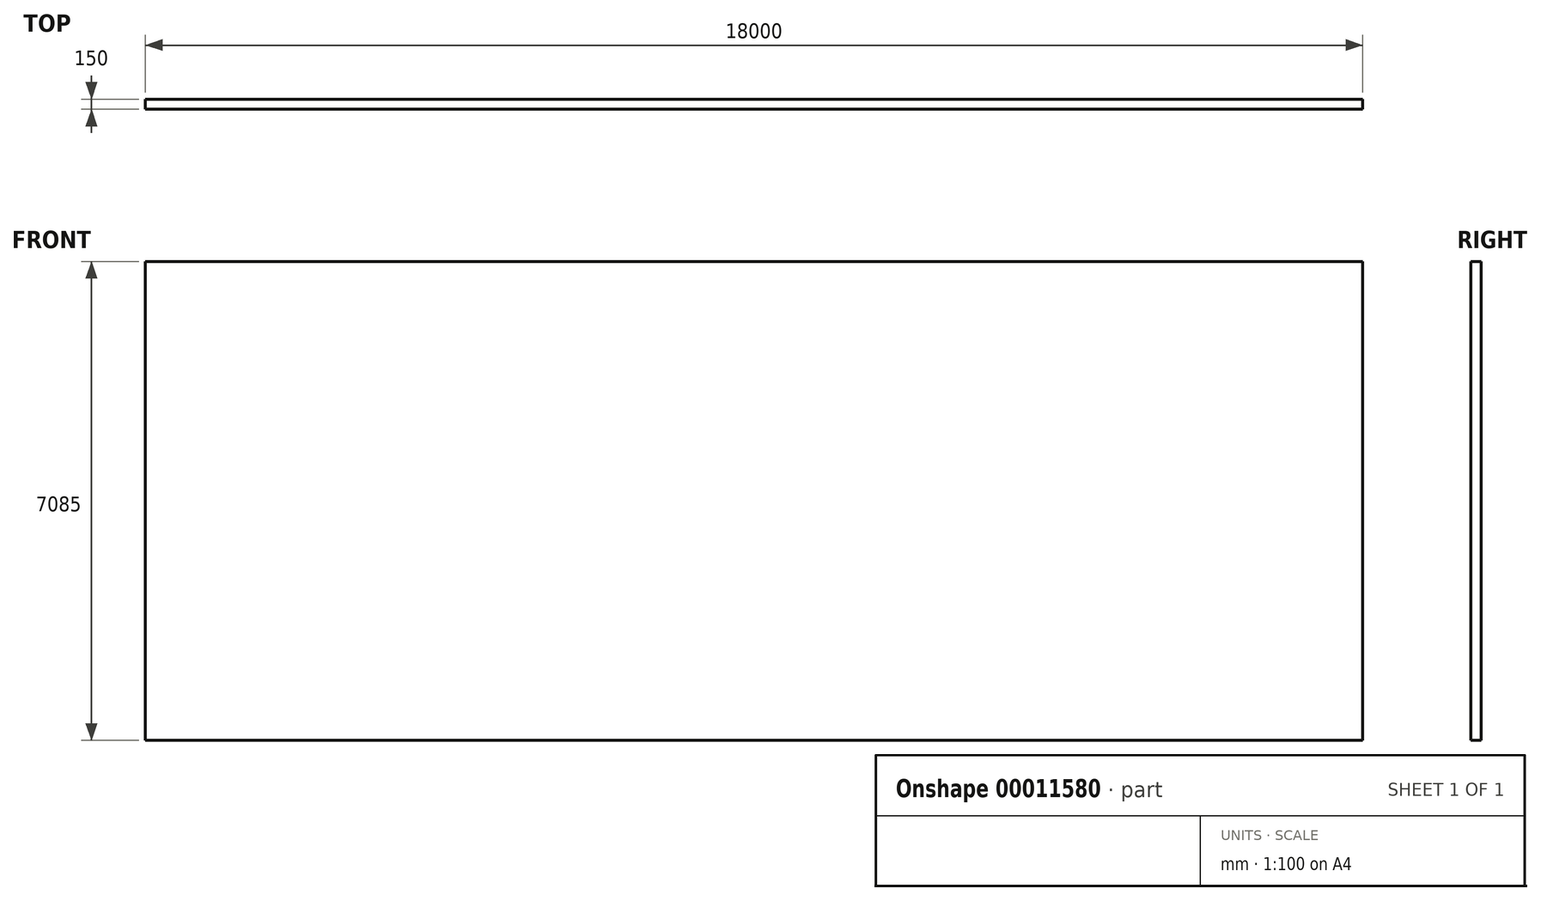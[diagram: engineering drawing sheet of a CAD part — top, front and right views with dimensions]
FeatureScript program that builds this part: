
annotation { "Feature Type Name" : "Feature", "Feature Type Description" : "" }
export const myFeature = defineFeature(function(context is Context, id is Id, definition is map)
    precondition{}
    {
        {
            var Q0;
            Q0=qCreatedBy(makeId("Top.planeOp"),FACE);
            var sketch = newSketch(context, id + "F0", { "sketchPlane" : qUnion([Q0])});
            skLineSegment(sketch, "E0.rect.bottom", {"start": v(-9000, 75) * mm, "end": v(9000, 75) * mm});
            skLineSegment(sketch, "E0.rect.top", {"start": v(-9000, -75) * mm, "end": v(9000, -75) * mm});
            skLineSegment(sketch, "E0.rect.left", {"start": v(-9000, 75) * mm, "end": v(-9000, -75) * mm});
            skLineSegment(sketch, "E0.rect.right", {"start": v(9000, 75) * mm, "end": v(9000, -75) * mm});
            skPoint(sketch, "E0.rect.middle", {"position": v(0, 0) * mm});
            skSolve(sketch);
        }
        {
            var Q0;
            Q0 = qSketchRegion(id + "F0", true);
            extrude(context, id + "F1", {"entities" : qUnion([Q0]), "depth" : 7085 * mm});
        }
    });
